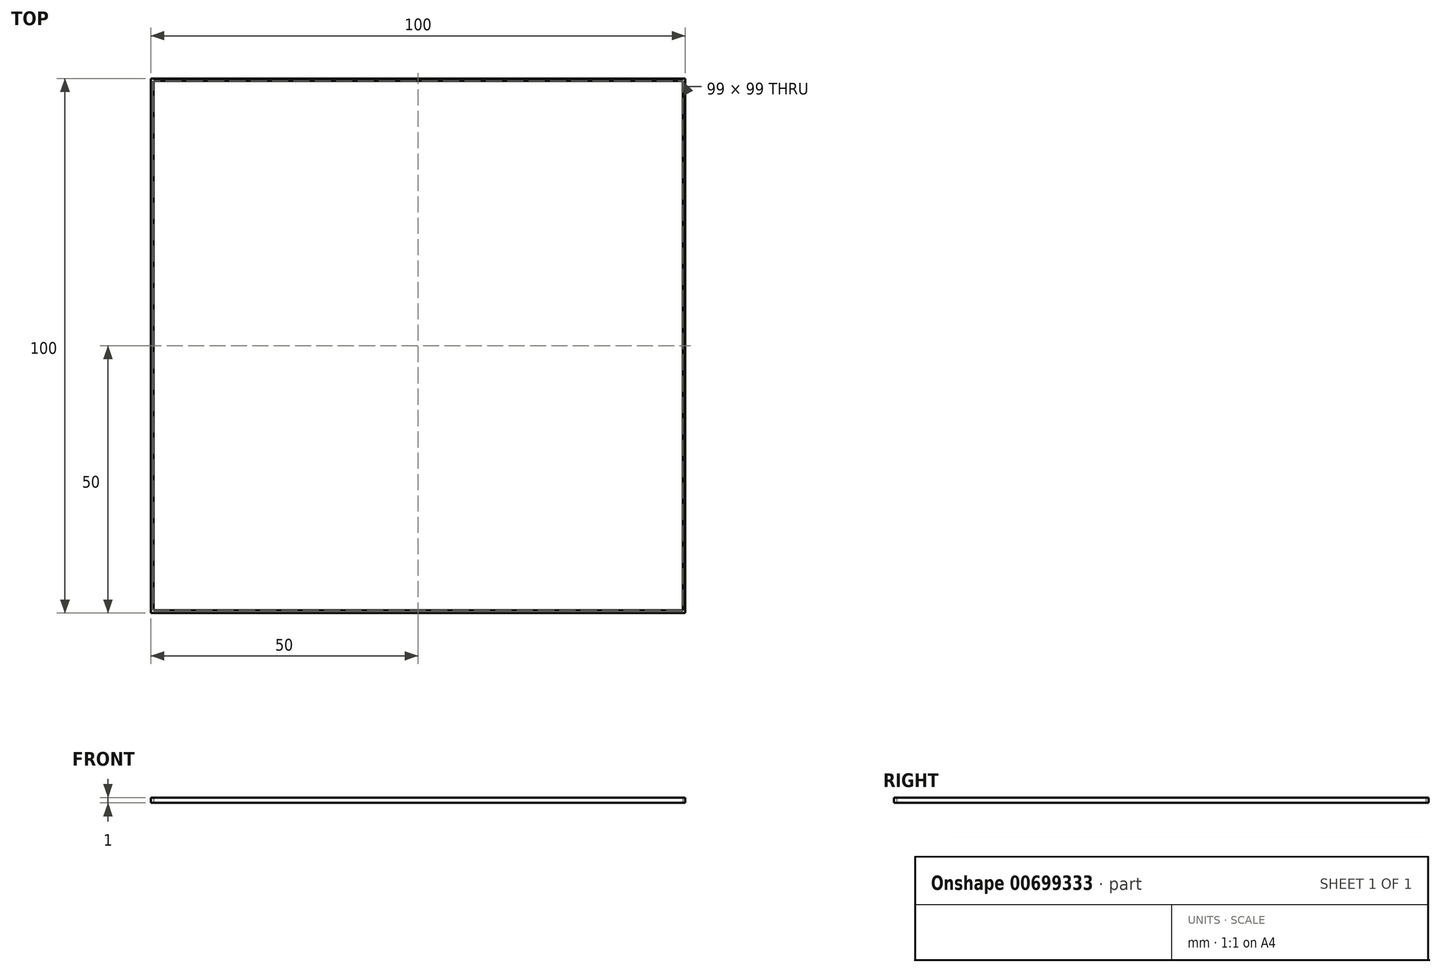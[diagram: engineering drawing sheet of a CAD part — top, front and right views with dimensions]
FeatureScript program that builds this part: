
annotation { "Feature Type Name" : "Feature", "Feature Type Description" : "" }
export const myFeature = defineFeature(function(context is Context, id is Id, definition is map)
    precondition{}
    {
        {
            var Q0;
            Q0=qCreatedBy(makeId("Top.planeOp"),FACE);
            var sketch = newSketch(context, id + "F0", { "sketchPlane" : qUnion([Q0])});
            skLineSegment(sketch, "E0.bottom", {"start": v(50, -50) * mm, "end": v(-50, -50) * mm});
            skLineSegment(sketch, "E0.top", {"start": v(50, 50) * mm, "end": v(-50, 50) * mm});
            skLineSegment(sketch, "E0.left", {"start": v(50, -50) * mm, "end": v(50, 50) * mm});
            skLineSegment(sketch, "E0.right", {"start": v(-50, -50) * mm, "end": v(-50, 50) * mm});
            skPoint(sketch, "E0.middle", {"position": v(0, 0) * mm});
            skLineSegment(sketch, "E1.bottom", {"start": v(49.5, -49.5) * mm, "end": v(-49.5, -49.5) * mm});
            skLineSegment(sketch, "E1.top", {"start": v(49.5, 49.5) * mm, "end": v(-49.5, 49.5) * mm});
            skLineSegment(sketch, "E1.left", {"start": v(49.5, -49.5) * mm, "end": v(49.5, 49.5) * mm});
            skLineSegment(sketch, "E1.right", {"start": v(-49.5, -49.5) * mm, "end": v(-49.5, 49.5) * mm});
            skSolve(sketch);
        }
        {
            var Q0;
            Q0=makeQuery(id+"F0.imprint","IMPRINT",FACE,{"disambiguationData":[TD([[makeQuery(id+"F0.imprint","IMPRINT",EDGE,{"derivedFrom":sQuery(id+"F0.wireOp",EDGE,"E0.bottom")}),-1.0]])]});
            extrude(context, id + "F1", {"entities" : qUnion([Q0]), "depth" : 1 * mm, "offsetDistance" : 25 * mm});
        }
    });
